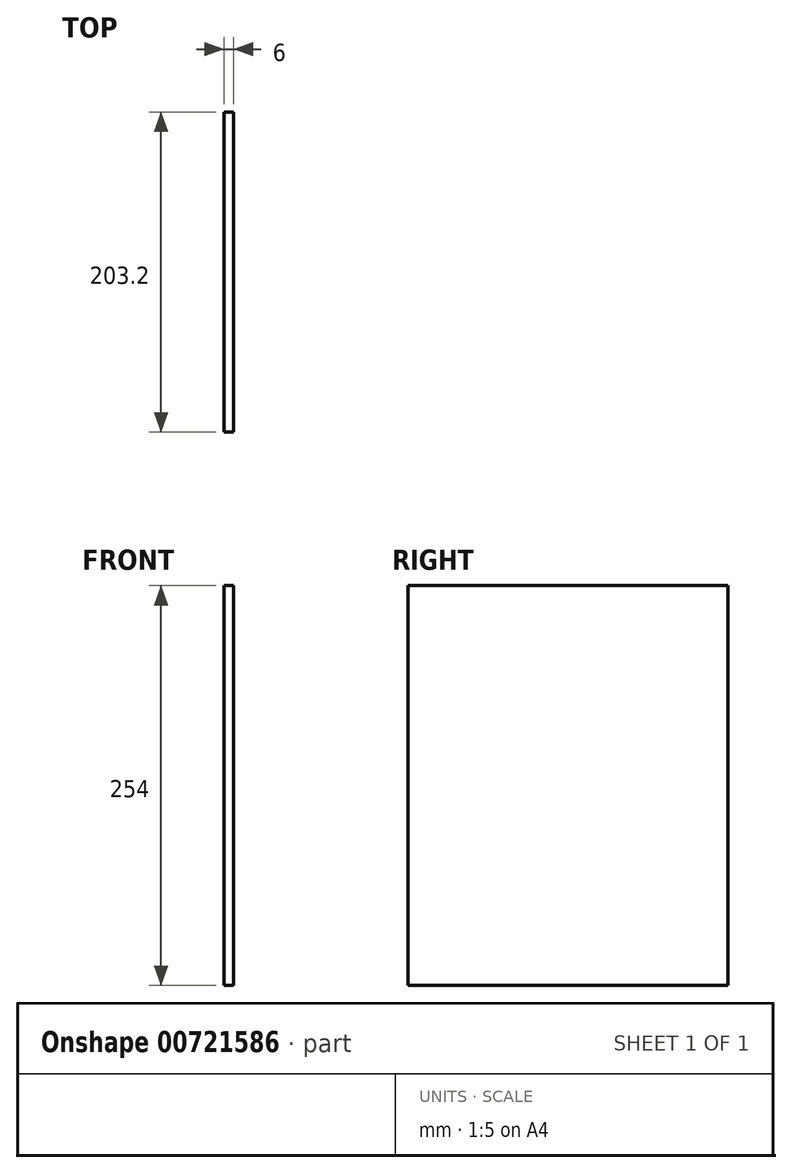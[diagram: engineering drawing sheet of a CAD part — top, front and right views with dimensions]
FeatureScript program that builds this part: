
annotation { "Feature Type Name" : "Feature", "Feature Type Description" : "" }
export const myFeature = defineFeature(function(context is Context, id is Id, definition is map)
    precondition{}
    {
        {
            var Q0;
            Q0=qCreatedBy(makeId("Right.planeOp"),FACE);
            var sketch = newSketch(context, id + "F0", { "sketchPlane" : qUnion([Q0])});
            skLineSegment(sketch, "E0.bottom", {"start": v(101.6, -127) * mm, "end": v(-101.6, -127) * mm});
            skLineSegment(sketch, "E0.top", {"start": v(101.6, 127) * mm, "end": v(-101.6, 127) * mm});
            skLineSegment(sketch, "E0.left", {"start": v(101.6, -127) * mm, "end": v(101.6, 127) * mm});
            skLineSegment(sketch, "E0.right", {"start": v(-101.6, -127) * mm, "end": v(-101.6, 127) * mm});
            skPoint(sketch, "E0.middle", {"position": v(0, 0) * mm});
            skSolve(sketch);
        }
        {
            var Q0;
            Q0=makeQuery(id+"F0.imprint","IMPRINT",FACE,{"disambiguationData":[TD([[makeQuery(id+"F0.imprint","IMPRINT",EDGE,{"derivedFrom":sQuery(id+"F0.wireOp",EDGE,"E0.bottom")}),-1.0]])]});
            extrude(context, id + "F1", {"entities" : qUnion([Q0]), "depth" : 6 * mm, "offsetDistance" : 25.4 * mm, "symmetric" : true});
        }
    });
